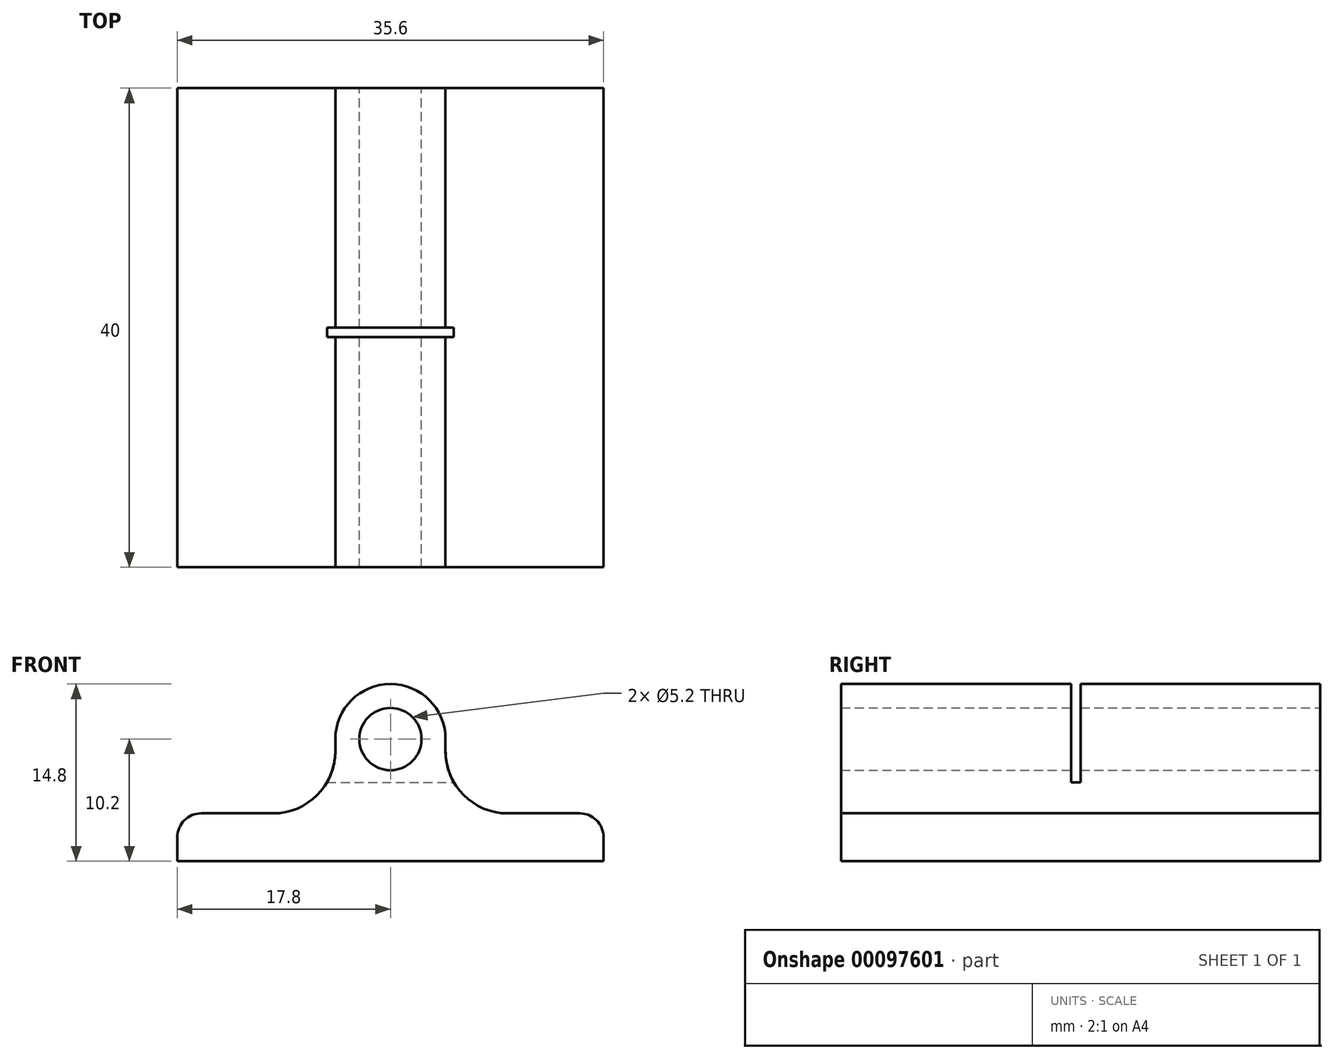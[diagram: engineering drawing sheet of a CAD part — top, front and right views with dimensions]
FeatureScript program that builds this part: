
annotation { "Feature Type Name" : "Feature", "Feature Type Description" : "" }
export const myFeature = defineFeature(function(context is Context, id is Id, definition is map)
    precondition{}
    {
        {
            var Q0;
            Q0=qCreatedBy(makeId("Front.planeOp"),FACE);
            var sketch = newSketch(context, id + "F0", { "sketchPlane" : qUnion([Q0])});
            skLineSegment(sketch, "E0.bottom", {"start": v(-17.8, 0) * mm, "end": v(17.8, 0) * mm});
            skLineSegment(sketch, "E0.top", {"start": v(-17.8, 4) * mm, "end": v(-9.8, 4) * mm});
            skLineSegment(sketch, "E0.left", {"start": v(-17.8, 0) * mm, "end": v(-17.8, 4) * mm});
            skLineSegment(sketch, "E0.right", {"start": v(17.8, 0) * mm, "end": v(17.8, 4) * mm});
            skLineSegment(sketch, "E1.top", {"start": v(-4.6, 10.2) * mm, "end": v(4.6, 10.2) * mm, "construction": true});
            skLineSegment(sketch, "E1.left", {"start": v(-4.6, 9.2) * mm, "end": v(-4.6, 10.2) * mm});
            skLineSegment(sketch, "E1.right", {"start": v(4.6, 9.2) * mm, "end": v(4.6, 10.2) * mm});
            skCircle(sketch, "E2", {"center": v(0, 10.2) * mm, "radius": 2.6 * mm});
            skLineSegment(sketch, "E3.trimOffspring", {"start": v(9.8, 4) * mm, "end": v(17.8, 4) * mm});
            skPoint(sketch, "E4.visualSharp", {"position": v(-4.6, 4) * mm});
            skArc(sketch, "E4.filletArc", {"start": v(-9.8, 4) * mm, "mid": v(-6.12, 5.52) * mm, "end": v(-4.6, 9.2) * mm});
            skPoint(sketch, "E5.visualSharp", {"position": v(4.6, 4) * mm});
            skArc(sketch, "E5.filletArc", {"start": v(4.6, 9.2) * mm, "mid": v(6.12, 5.52) * mm, "end": v(9.8, 4) * mm});
            skArc(sketch, "E6", {"start": v(-4.6, 10.2) * mm, "mid": v(0, 5.6) * mm, "end": v(4.6, 10.2) * mm, "construction": true});
            skArc(sketch, "E7", {"start": v(4.6, 10.2) * mm, "mid": v(0, 14.8) * mm, "end": v(-4.6, 10.2) * mm});
            skSolve(sketch);
        }
        {
            var Q0;
            Q0=makeQuery(id+"F0.imprint","IMPRINT",FACE,{"disambiguationData":[TD([[makeQuery(id+"F0.imprint","IMPRINT",EDGE,{"derivedFrom":sQuery(id+"F0.wireOp",EDGE,"E0.bottom")}),1.0]])]});
            extrude(context, id + "F1", {"entities" : qUnion([Q0]), "depth" : 40 * mm});
        }
        {
            var Q0;
            Q0=makeQuery(id+"F1.opExtrude","SWEPT_FACE",FACE,{"disambiguationData":[OSD([sQuery(id+"F0.wireOp",EDGE,"E0.right")])]});
            var sketch = newSketch(context, id + "F2", { "sketchPlane" : qUnion([Q0])});
            skLineSegment(sketch, "E8.1", {"start": v(-40, 4) * mm, "end": v(0, 4) * mm, "construction": true});
            skLineSegment(sketch, "E9", {"start": v(-40, 14.8) * mm, "end": v(0, 14.8) * mm, "construction": true});
            skLineSegment(sketch, "E10.bottom", {"start": v(-20, 14.8) * mm, "end": v(-20.8, 14.8) * mm});
            skLineSegment(sketch, "E10.top", {"start": v(-20, 4) * mm, "end": v(-20.8, 4) * mm});
            skLineSegment(sketch, "E10.left", {"start": v(-20, 14.8) * mm, "end": v(-20, 6.6) * mm});
            skLineSegment(sketch, "E10.right", {"start": v(-20.8, 14.8) * mm, "end": v(-20.8, 6.6) * mm});
            skLineSegment(sketch, "E11", {"start": v(-20.8, 6.6) * mm, "end": v(-20, 6.6) * mm});
            skSolve(sketch);
        }
        {
            var Q0;
            Q0=makeQuery(id+"F2.imprint","IMPRINT",FACE,{"disambiguationData":[TD([[makeQuery(id+"F2.imprint","IMPRINT",EDGE,{"derivedFrom":sQuery(id+"F2.wireOp",EDGE,"E10.bottom")}),1.0]])]});
            extrude(context, id + "F3", {"entities" : qUnion([Q0]), "operationType" : NewBodyOperationType.REMOVE, "endBound" : BoundingType.THROUGH_ALL, "oppositeDirection" : true, "depth" : 25 * mm});
        }
        {
            var Q0;
            Q0=makeQuery(id+"F1.opExtrude","SWEPT_EDGE",EDGE,{"disambiguationData":[OSD([sQuery(id+"F0.wireOp",EDGE,"E0.top"),sQuery(id+"F0.wireOp",EDGE,"E0.left")])]});
            var Q1;
            Q1=makeQuery(id+"F1.opExtrude","SWEPT_EDGE",EDGE,{"disambiguationData":[OSD([sQuery(id+"F0.wireOp",EDGE,"E0.right"),sQuery(id+"F0.wireOp",EDGE,"E3.trimOffspring")])]});
            fillet(context, id + "F4", {"entities" : qUnion([Q0, Q1]), "radius" : 2 * mm, "tangentPropagation" : true, "allowEdgeOverflow" : false});
        }
    });
